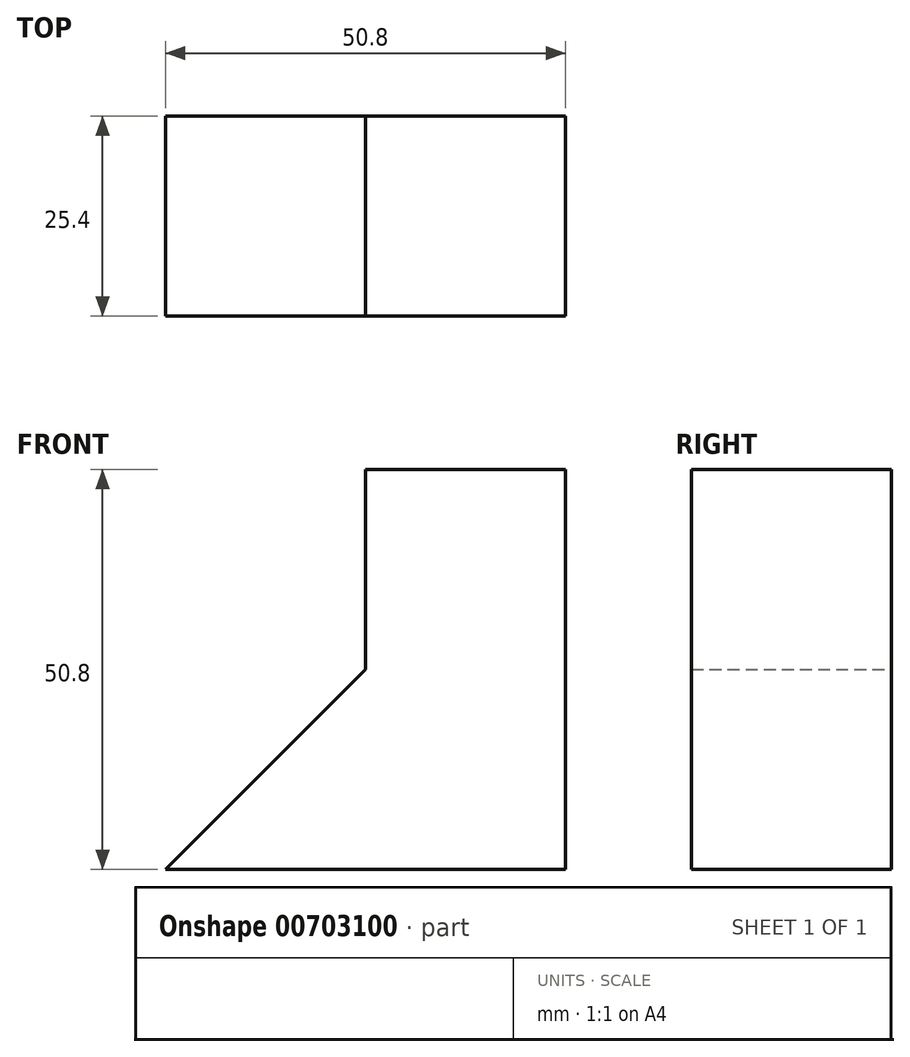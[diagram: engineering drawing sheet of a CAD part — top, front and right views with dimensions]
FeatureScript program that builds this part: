
annotation { "Feature Type Name" : "Feature", "Feature Type Description" : "" }
export const myFeature = defineFeature(function(context is Context, id is Id, definition is map)
    precondition{}
    {
        {
            var Q0;
            Q0=qCreatedBy(makeId("Front.planeOp"),FACE);
            var sketch = newSketch(context, id + "F0", { "sketchPlane" : qUnion([Q0])});
            skLineSegment(sketch, "E0", {"start": v(-45.92, 31.98) * mm, "end": v(-20.52, 31.98) * mm});
            skLineSegment(sketch, "E1", {"start": v(-45.92, 31.98) * mm, "end": v(-45.92, 6.58) * mm});
            skLineSegment(sketch, "E2", {"start": v(-20.52, 31.98) * mm, "end": v(-20.52, -18.82) * mm});
            skLineSegment(sketch, "E3", {"start": v(-20.52, -18.82) * mm, "end": v(-71.32, -18.82) * mm});
            skLineSegment(sketch, "E4", {"start": v(-71.32, -18.82) * mm, "end": v(-45.92, 6.58) * mm});
            skSolve(sketch);
        }
        {
            var Q0;
            Q0=makeQuery(id+"F0.imprint","IMPRINT",FACE,{"disambiguationData":[TD([[makeQuery(id+"F0.imprint","IMPRINT",EDGE,{"derivedFrom":sQuery(id+"F0.wireOp",EDGE,"E0")}),-1.0]])]});
            extrude(context, id + "F1", {"entities" : qUnion([Q0]), "depth" : 25.4 * mm, "offsetDistance" : 25.4 * mm});
        }
    });
